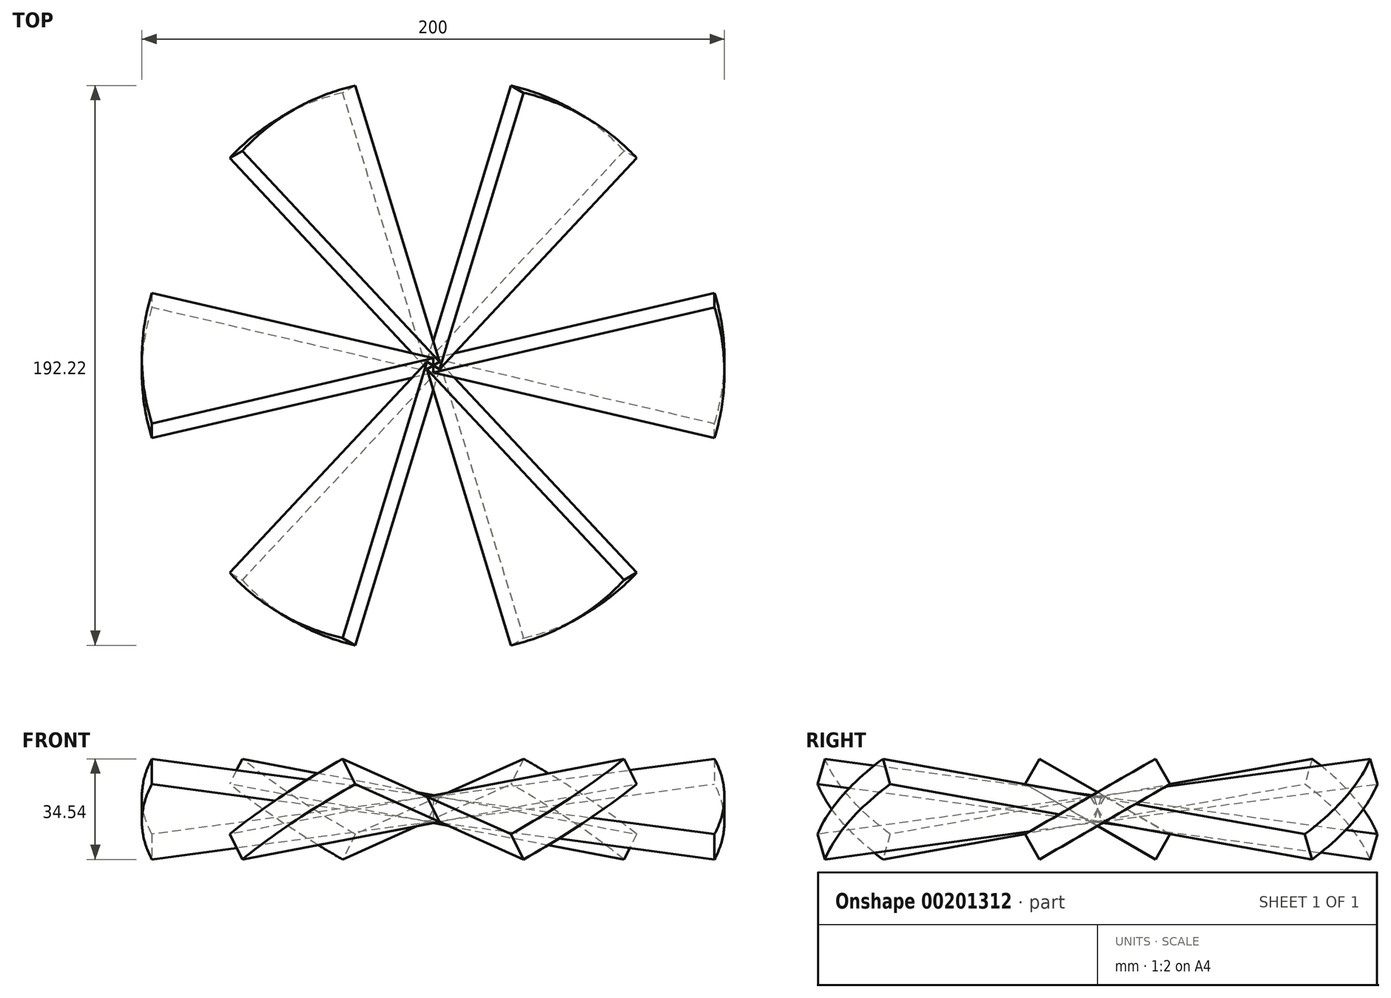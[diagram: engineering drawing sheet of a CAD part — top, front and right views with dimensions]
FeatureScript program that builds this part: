
annotation { "Feature Type Name" : "Feature", "Feature Type Description" : "" }
export const myFeature = defineFeature(function(context is Context, id is Id, definition is map)
    precondition{}
    {
        {
            var Q0;
            Q0=qCreatedBy(makeId("Top.planeOp"),FACE);
            var sketch = newSketch(context, id + "F0", { "sketchPlane" : qUnion([Q0])});
            skLineSegment(sketch, "E0", {"start": v(0, 0) * mm, "end": v(96.6, 25.88) * mm});
            skLineSegment(sketch, "E1.MirrorCS", {"start": v(0, 0) * mm, "end": v(96.6, -25.88) * mm});
            skArc(sketch, "E2", {"start": v(96.6, 25.88) * mm, "mid": v(100, 0) * mm, "end": v(96.6, -25.88) * mm});
            skSolve(sketch);
        }
        {
            var Q0;
            Q0=makeQuery(id+"F0.imprint","IMPRINT",FACE,{"disambiguationData":[TD([[makeQuery(id+"F0.imprint","IMPRINT",EDGE,{"derivedFrom":sQuery(id+"F0.wireOp",EDGE,"E0")}),-1.0]])]});
            extrude(context, id + "F1", {"entities" : qUnion([Q0]), "endBound" : BoundingType.SYMMETRIC, "depth" : 10 * mm});
        }
        {
            var Q0;
            Q0=qCreatedBy(makeId("Top.planeOp"),FACE);
            var sketch = newSketch(context, id + "F2", { "sketchPlane" : qUnion([Q0])});
            skLineSegment(sketch, "E3", {"start": v(-57.7, 0) * mm, "end": v(70.5, 0) * mm});
            skSolve(sketch);
        }
        {
            var Q0;
            Q0=makeQuery(id+"F1.opExtrude","SWEPT_BODY",BODY,{"disambiguationData":[OSD([sQuery(id+"F0.wireOp",EDGE,"E0"),sQuery(id+"F0.wireOp",EDGE,"E1.MirrorCS"),sQuery(id+"F0.wireOp",EDGE,"E2")])]});
            var Q1;
            Q1=sQuery(id+"F2.wireOp",EDGE,"E3");
            transform(context, id + "F3", {"entities" : qUnion([Q0]), "transformType" : TransformType.ROTATION, "transformAxis" : qUnion([Q1]), "angle" : 30 * degree, "makeCopy" : false});
        }
        {
            var Q0;
            Q0=qCreatedBy(makeId("Front.planeOp"),FACE);
            var sketch = newSketch(context, id + "F4", { "sketchPlane" : qUnion([Q0])});
            skLineSegment(sketch, "E4", {"start": v(0, 0) * mm, "end": v(0, 53.12) * mm});
            skSolve(sketch);
        }
        {
            var Q0;
            Q0=makeQuery(id+"F1.opExtrude","SWEPT_BODY",BODY,{"disambiguationData":[OSD([sQuery(id+"F0.wireOp",EDGE,"E0"),sQuery(id+"F0.wireOp",EDGE,"E1.MirrorCS"),sQuery(id+"F0.wireOp",EDGE,"E2")])]});
            var Q1;
            Q1=sQuery(id+"F4.wireOp",EDGE,"E4");
            circularPattern(context, id + "F5", {"entities" : qUnion([Q0]), "axis" : qUnion([Q1]), "angle" : 360 * degree, "instanceCount" : 6, "equalSpace" : true});
        }
        {
            var Q0;
            Q0=qCreatedBy(makeId("Top.planeOp"),FACE);
            var sketch = newSketch(context, id + "F6", { "sketchPlane" : qUnion([Q0])});
            skCircle(sketch, "E5", {"center": v(0, 0) * mm, "radius": 30 * mm});
            skSolve(sketch);
        }
        {
            var Q0;
            Q0 = qSketchRegion(id + "F6", true);
            var Q1;
            Q1=sQuery(id+"F6.wireOp",EDGE,"E5");
            extrude(context, id + "F7", {"entities" : qUnion([Q0]), "bodyType" : ToolBodyType.SURFACE, "surfaceEntities" : qUnion([Q1]), "endBound" : BoundingType.SYMMETRIC, "depth" : 25 * mm});
        }
    });
